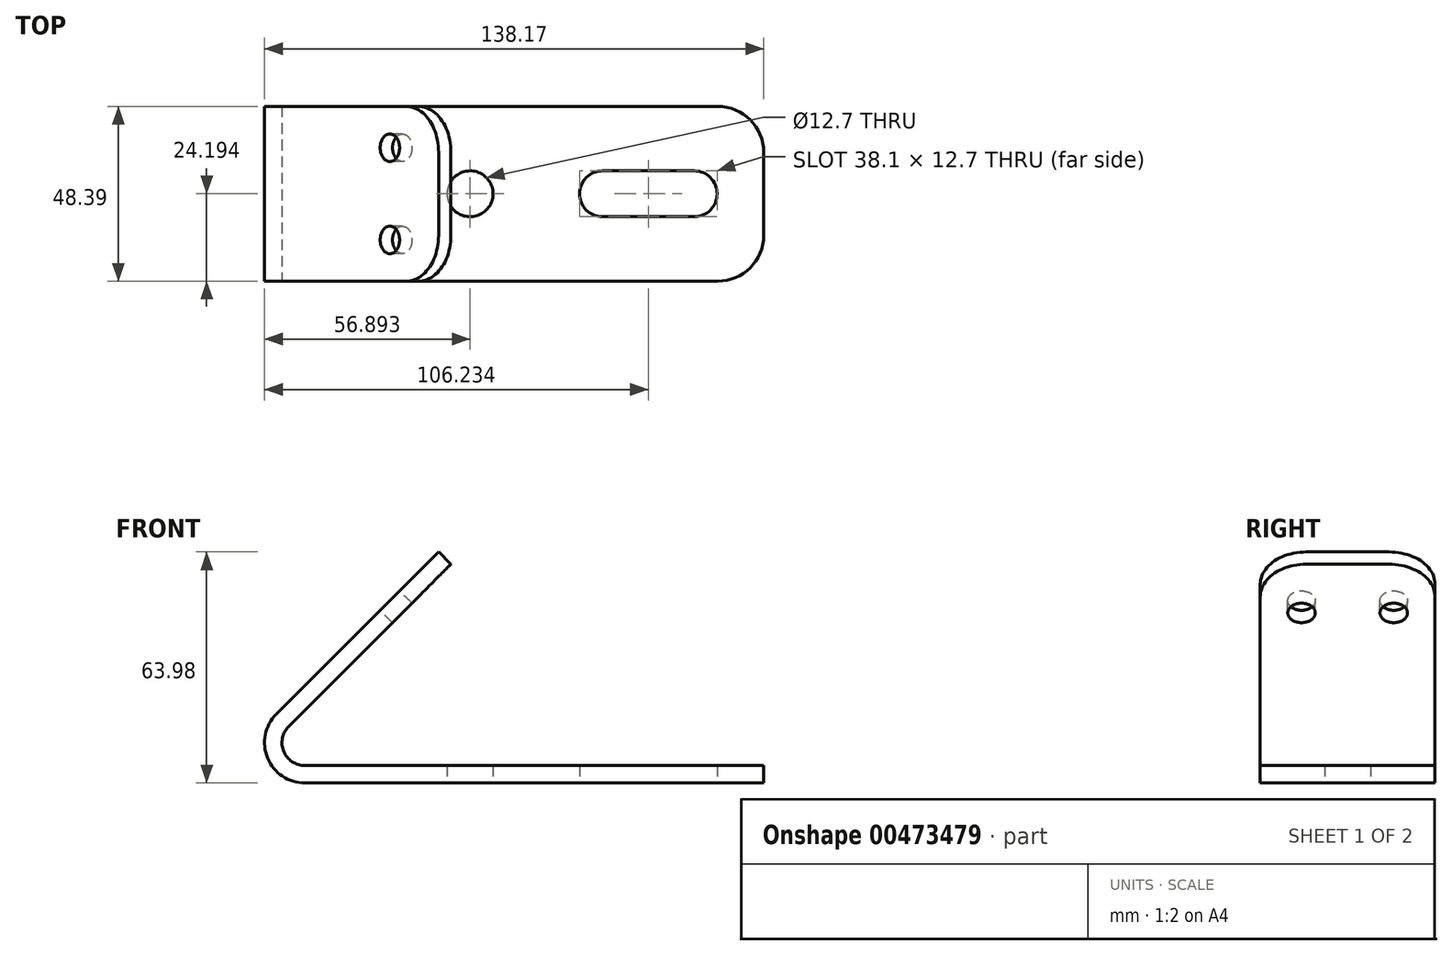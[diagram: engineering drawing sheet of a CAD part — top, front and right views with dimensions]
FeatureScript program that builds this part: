
annotation { "Feature Type Name" : "Feature", "Feature Type Description" : "" }
export const myFeature = defineFeature(function(context is Context, id is Id, definition is map)
    precondition{}
    {
        {
            var Q0;
            Q0=qCreatedBy(makeId("Front.planeOp"),FACE);
            var sketch = newSketch(context, id + "F0", { "sketchPlane" : qUnion([Q0])});
            skLineSegment(sketch, "E0", {"start": v(77.8, 0) * mm, "end": v(-49.2, 0) * mm});
            skLineSegment(sketch, "E1", {"start": v(77.8, 4.83) * mm, "end": v(-49.2, 4.83) * mm});
            skLineSegment(sketch, "E2", {"start": v(77.8, 4.83) * mm, "end": v(77.8, 0) * mm});
            skLineSegment(sketch, "E3", {"start": v(-53.7, 15.67) * mm, "end": v(-8.8, 60.57) * mm});
            skLineSegment(sketch, "E4", {"start": v(-57.1, 19.08) * mm, "end": v(-12.2, 63.98) * mm});
            skLineSegment(sketch, "E5", {"start": v(-12.2, 63.98) * mm, "end": v(-8.8, 60.57) * mm});
            skArc(sketch, "E6", {"start": v(-57.1, 19.08) * mm, "mid": v(-59.53, 6.9) * mm, "end": v(-49.2, 0) * mm});
            skArc(sketch, "E7", {"start": v(-53.7, 15.67) * mm, "mid": v(-55.07, 8.75) * mm, "end": v(-49.2, 4.83) * mm});
            skSolve(sketch);
        }
        {
            var Q0;
            Q0=makeQuery(id+"F0.imprint","IMPRINT",FACE,{"disambiguationData":[TD([[makeQuery(id+"F0.imprint","IMPRINT",EDGE,{"derivedFrom":sQuery(id+"F0.wireOp",EDGE,"E0")}),-1.0]])]});
            extrude(context, id + "F1", {"entities" : qUnion([Q0]), "oppositeDirection" : true, "depth" : 48.4 * mm});
        }
        {
            var Q0;
            Q0=makeQuery(id+"F1.opExtrude","CAP_EDGE",EDGE,{"disambiguationData":[OSD([sQuery(id+"F0.wireOp",EDGE,"E5")])],"isStart":false});
            var Q1;
            Q1=makeQuery(id+"F1.opExtrude","CAP_EDGE",EDGE,{"disambiguationData":[OSD([sQuery(id+"F0.wireOp",EDGE,"E5")])],"isStart":true});
            var Q2;
            Q2=makeQuery(id+"F1.opExtrude","CAP_EDGE",EDGE,{"disambiguationData":[OSD([sQuery(id+"F0.wireOp",EDGE,"E2")])],"isStart":true});
            var Q3;
            Q3=makeQuery(id+"F1.opExtrude","CAP_EDGE",EDGE,{"disambiguationData":[OSD([sQuery(id+"F0.wireOp",EDGE,"E2")])],"isStart":false});
            fillet(context, id + "F2", {"entities" : qUnion([Q0, Q1, Q2, Q3]), "radius" : 12.7 * mm, "tangentPropagation" : true, "allowEdgeOverflow" : false});
        }
        {
            var Q0;
            Q0=makeQuery(id+"F1.opExtrude","SWEPT_FACE",FACE,{"disambiguationData":[OSD([sQuery(id+"F0.wireOp",EDGE,"E4")])]});
            var sketch = newSketch(context, id + "F3", { "sketchPlane" : qUnion([Q0])});
            skPoint(sketch, "E8", {"position": v(-36.96, 17.56) * mm});
            skPoint(sketch, "E9", {"position": v(-11.43, 17.56) * mm});
            skSolve(sketch);
        }
        {
            var Q0;
            Q0=sQuery(id+"F3.wireOp",VERTEX,"E8");
            var Q1;
            Q1=sQuery(id+"F3.wireOp",VERTEX,"E9");
            var Q2;
            Q2=makeQuery(id+"F1.opExtrude","SWEPT_BODY",BODY,{"disambiguationData":[OSD([sQuery(id+"F0.wireOp",EDGE,"E0"),sQuery(id+"F0.wireOp",EDGE,"E1"),sQuery(id+"F0.wireOp",EDGE,"E2"),sQuery(id+"F0.wireOp",EDGE,"E3"),sQuery(id+"F0.wireOp",EDGE,"E4"),sQuery(id+"F0.wireOp",EDGE,"E5"),sQuery(id+"F0.wireOp",EDGE,"E6"),sQuery(id+"F0.wireOp",EDGE,"E7")])]});
            hole(context, id + "F4", {"style" : HoleStyle.SIMPLE, "endStyle" : HoleEndStyle.BLIND, "holeDiameter" : 7.62 * mm, "holeDepth" : 12.7 * mm, "isTappedThrough" : true, "tappedDepth" : 12.7 * mm, "tapClearance" : 3, "locations" : qUnion([Q0, Q1]), "scope" : qUnion([Q2])});
        }
        {
            var Q0;
            Q0=makeQuery(id+"F1.opExtrude","SWEPT_FACE",FACE,{"disambiguationData":[OSD([sQuery(id+"F0.wireOp",EDGE,"E0")])]});
            var sketch = newSketch(context, id + "F5", { "sketchPlane" : qUnion([Q0])});
            skPoint(sketch, "E10", {"position": v(-3.49, -24.2) * mm});
            skLineSegment(sketch, "E11", {"start": v(-3.49, -24.2) * mm, "end": v(-3.49, -48.39) * mm});
            skLineSegment(sketch, "E12", {"start": v(-3.49, -48.39) * mm, "end": v(-3.49, -24.2) * mm});
            skLineSegment(sketch, "E13", {"start": v(-3.49, 0) * mm, "end": v(-3.49, -24.2) * mm});
            skLineSegment(sketch, "E14.bottom", {"start": v(33.15, -17.84) * mm, "end": v(58.55, -17.84) * mm});
            skLineSegment(sketch, "E14.top", {"start": v(33.15, -30.54) * mm, "end": v(58.55, -30.54) * mm});
            skPoint(sketch, "E14.middle", {"position": v(45.85, -24.2) * mm});
            skArc(sketch, "E15", {"start": v(58.55, -30.54) * mm, "mid": v(64.9, -24.2) * mm, "end": v(58.55, -17.84) * mm});
            skArc(sketch, "E16", {"start": v(33.15, -17.84) * mm, "mid": v(26.8, -24.2) * mm, "end": v(33.15, -30.54) * mm});
            skSolve(sketch);
        }
        {
            var Q0;
            Q0=sQuery(id+"F5.wireOp",VERTEX,"E10");
            var Q1;
            Q1=makeQuery(id+"F1.opExtrude","SWEPT_BODY",BODY,{"disambiguationData":[OSD([sQuery(id+"F0.wireOp",EDGE,"E0"),sQuery(id+"F0.wireOp",EDGE,"E1"),sQuery(id+"F0.wireOp",EDGE,"E2"),sQuery(id+"F0.wireOp",EDGE,"E3"),sQuery(id+"F0.wireOp",EDGE,"E4"),sQuery(id+"F0.wireOp",EDGE,"E5"),sQuery(id+"F0.wireOp",EDGE,"E6"),sQuery(id+"F0.wireOp",EDGE,"E7")])]});
            hole(context, id + "F6", {"style" : HoleStyle.SIMPLE, "endStyle" : HoleEndStyle.BLIND, "holeDiameter" : 12.7 * mm, "holeDepth" : 12.7 * mm, "isTappedThrough" : true, "tappedDepth" : 12.7 * mm, "tapClearance" : 3, "locations" : qUnion([Q0]), "scope" : qUnion([Q1])});
        }
        {
            var Q0;
            Q0=makeQuery(id+"F5.imprint","IMPRINT",FACE,{"disambiguationData":[TD([[makeQuery(id+"F5.imprint","IMPRINT",EDGE,{"derivedFrom":sQuery(id+"F5.wireOp",EDGE,"E14.bottom")}),-1.0]])]});
            extrude(context, id + "F7", {"entities" : qUnion([Q0]), "operationType" : NewBodyOperationType.REMOVE, "endBound" : BoundingType.THROUGH_ALL, "oppositeDirection" : true, "depth" : 25.4 * mm});
        }
    });
